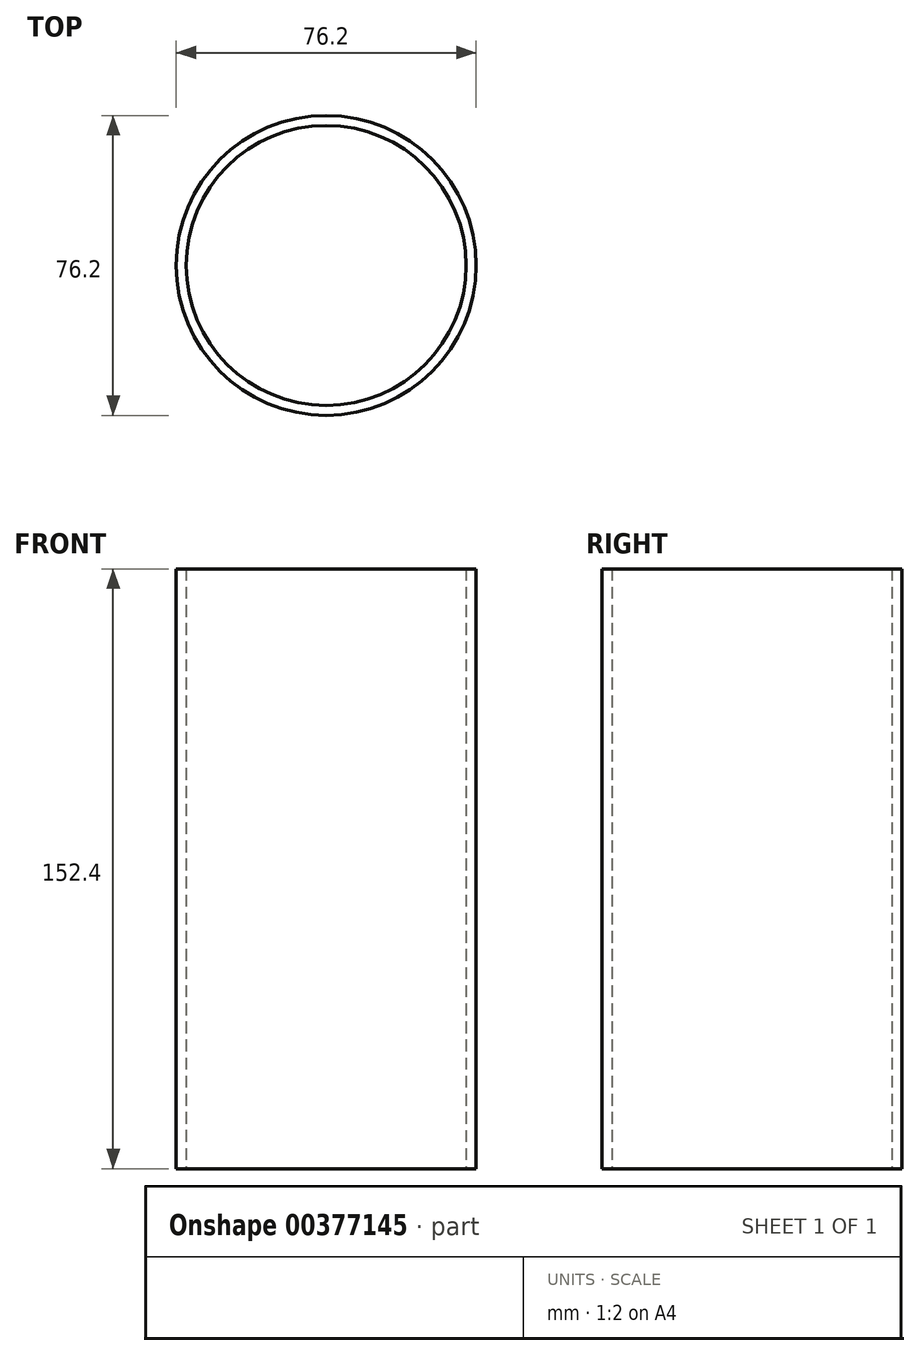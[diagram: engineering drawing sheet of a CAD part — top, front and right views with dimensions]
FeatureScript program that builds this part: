
annotation { "Feature Type Name" : "Feature", "Feature Type Description" : "" }
export const myFeature = defineFeature(function(context is Context, id is Id, definition is map)
    precondition{}
    {
        {
            var Q0;
            Q0=qCreatedBy(makeId("Top.planeOp"),FACE);
            var sketch = newSketch(context, id + "F0", { "sketchPlane" : qUnion([Q0])});
            skCircle(sketch, "E0", {"center": v(0, 0) * mm, "radius": 38.1 * mm});
            skCircle(sketch, "E1", {"center": v(0, 0) * mm, "radius": 35.56 * mm});
            skSolve(sketch);
        }
        {
            var Q0;
            Q0=makeQuery(id+"F0.imprint","IMPRINT",FACE,{"disambiguationData":[TD([[makeQuery(id+"F0.imprint","IMPRINT",EDGE,{"derivedFrom":sQuery(id+"F0.wireOp",EDGE,"E0")}),1.0]])]});
            extrude(context, id + "F1", {"entities" : qUnion([Q0]), "depth" : 152.4 * mm});
        }
    });
